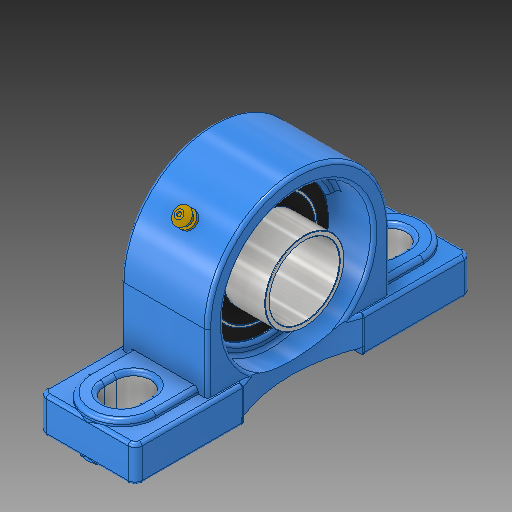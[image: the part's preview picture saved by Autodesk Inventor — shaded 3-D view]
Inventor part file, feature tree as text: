
AUTODESK INVENTOR PART (.ipt)
format: ipt  version: 2019 (Build 230136000, 136)  size: 668,160 bytes
history: native  units: in
note: dims shown in document units (in); Inventor stores cm internally (conversion verified against a paired STEP export)
features: sketch x28, plane x7, other x3
ambient origin geometry x8: Origin, YZ Plane, XZ Plane, XY Plane, X Axis, Y Axis, Z Axis, Center Point
bodies: Solid1 (feature_tree)
feature tree (38):
  other  "Pillow Bearing inventor.ipt"
  other  "Solid1::Pillow Bearing inventor.ipt"
  other  "TaggingFeature1"
  sketch  "Sketch1"  dims[d0=0.3937in]
  sketch  "Sketch2"
  sketch  "Sketch3"
  sketch  "Sketch4"
  sketch  "Sketch5"
  sketch  "Sketch6"
  sketch  "Sketch7"
  sketch  "Sketch8"
  sketch  "Sketch9"
  sketch  "Sketch10"
  sketch  "Sketch11"
  sketch  "Sketch13"
  sketch  "Sketch14"
  sketch  "Sketch15"
  sketch  "Sketch17"
  sketch  "Sketch18"
  sketch  "Sketch19"
  sketch  "Sketch20"
  sketch  "Sketch21"
  sketch  "Sketch22"
  sketch  "Sketch23"
  sketch  "Sketch24"
  sketch  "Sketch25"
  sketch  "Sketch26"
  sketch  "Sketch27"
  sketch  "Sketch28"
  sketch  "Sketch29"
  sketch  "Sketch30"
  plane  "Work Plane1"
  plane  "Work Plane2"
  plane  "Work Plane5"
  plane  "Work Plane6"
  plane  "Work Plane7"
  plane  "Work Plane8"
  plane  "Work Plane9"
